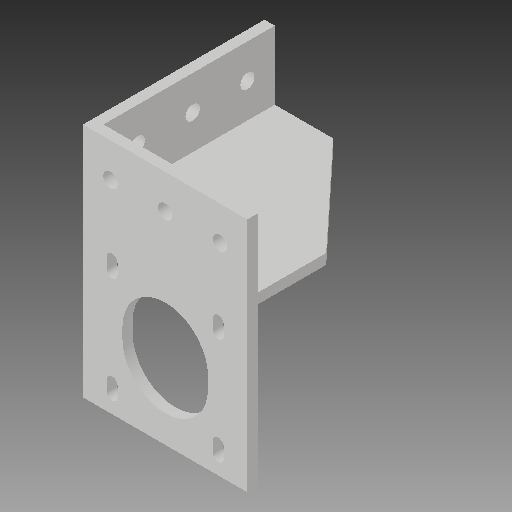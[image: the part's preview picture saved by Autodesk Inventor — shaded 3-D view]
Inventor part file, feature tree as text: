
AUTODESK INVENTOR PART (.ipt)
format: ipt  version: 2018 (Build 220112000, 112)  size: 226,816 bytes
history: native  units: in
note: dims shown in document units (in); Inventor stores cm internally (conversion verified against a paired STEP export)
features: extrude x8, sketch x8, projected_geometry x1
ambient origin geometry x8: Origin, YZ Plane, XZ Plane, XY Plane, X Axis, Y Axis, Z Axis, Center Point
bodies: Solid1 (feature_tree)
feature tree (17):
  extrude  "Extrusion1"  Depth=0.9055in
  extrude  "Extrusion2"  Depth=0.1181in TaperAngle=0.0deg
  sketch  "Sketch3"  dims[d6=1.8898in d7=1.811in]
  extrude  "Extrusion4"  Depth=1.811in
  extrude  "Extrusion8"  Depth=0.1181in
  extrude  "Extrusion9"  Depth=0.3346in
  extrude  "Extrusion10"  Depth=1.2205in
  extrude  "Extrusion11"  Depth=0.1181in TaperAngle=0.0deg
  extrude  "Extrusion12"  Depth=0.3937in
  sketch  "Sketch1"  dims[d0=0.9055in d1=0.9055in]
  sketch  "Sketch2"  dims[d2=1.8898in d4=0.1181in d5=0.0in]
  sketch  "Sketch4"  dims[d8=0.126in d9=0.1181in]
  projected_geometry  "Projected Loop1"
  sketch  "Sketch8"  dims[d10=0.3346in d11=0.1969in]
  sketch  "Sketch9"  dims[d12=1.2205in d13=1.2205in]
  sketch  "Sketch10"  dims[d14=0.1181in d15=0.2362in d16=0.0in]
  sketch  "Sketch11"  dims[d19=0.1654in d20=0.6299in d21=0.315in d23=0.6299in d30=0.1181in d31=1.9685in d32=0.0in d46=0.9843in d47=0.1181in d48=0.1181in d49=0.0in d50=0.1181in d51=0.0in d52=0.3937in d53=0.1181in d54=0.0in d55=0.7874in d56=0.7874in d57=0.1181in d58=0.0in d59=0.1654in d60=0.6299in d61=0.5118in d62=0.6299in d63=0.1181in d64=0.0in d65=0.3937in]
